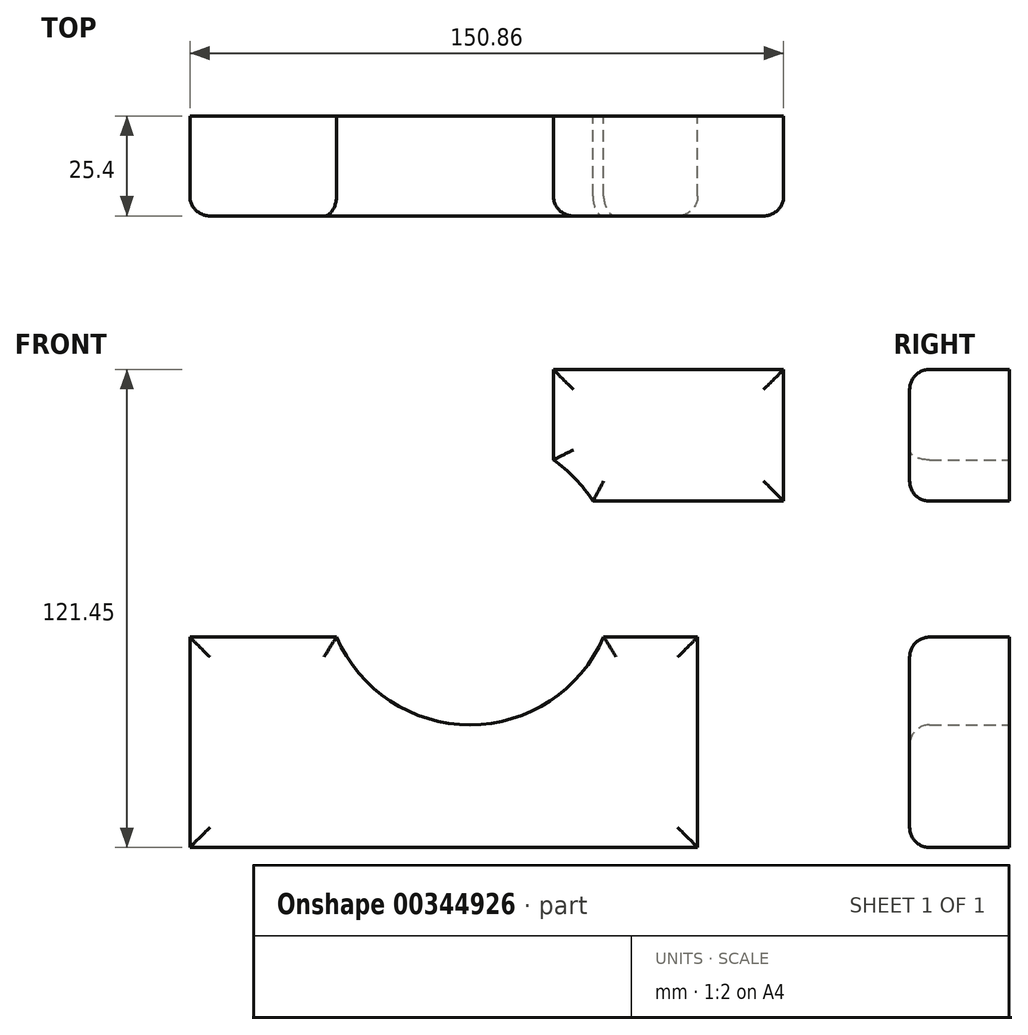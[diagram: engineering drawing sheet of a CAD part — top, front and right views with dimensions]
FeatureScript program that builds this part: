
annotation { "Feature Type Name" : "Feature", "Feature Type Description" : "" }
export const myFeature = defineFeature(function(context is Context, id is Id, definition is map)
    precondition{}
    {
        {
            var Q0;
            Q0=qCreatedBy(makeId("Front.planeOp"),FACE);
            var sketch = newSketch(context, id + "F0", { "sketchPlane" : qUnion([Q0])});
            skLineSegment(sketch, "E0.bottom", {"start": v(-71.2, -68.14) * mm, "end": v(57.8, -68.14) * mm});
            skLineSegment(sketch, "E0.top", {"start": v(-71.2, -14.68) * mm, "end": v(57.8, -14.68) * mm});
            skLineSegment(sketch, "E0.left", {"start": v(-71.2, -68.14) * mm, "end": v(-71.2, -14.68) * mm});
            skLineSegment(sketch, "E0.right", {"start": v(57.8, -68.14) * mm, "end": v(57.8, -14.68) * mm});
            skLineSegment(sketch, "E1.bottom", {"start": v(21.15, 19.85) * mm, "end": v(79.66, 19.85) * mm});
            skLineSegment(sketch, "E1.top", {"start": v(21.15, 53.31) * mm, "end": v(79.66, 53.31) * mm});
            skLineSegment(sketch, "E1.left", {"start": v(21.15, 19.85) * mm, "end": v(21.15, 53.31) * mm});
            skLineSegment(sketch, "E1.right", {"start": v(79.66, 19.85) * mm, "end": v(79.66, 53.31) * mm});
            skCircle(sketch, "E2", {"center": v(0, 0) * mm, "radius": 36.97 * mm});
            skSolve(sketch);
        }
        {
            var Q0;
            {var subQ2=sQuery(id+"F0.wireOp",EDGE,"E1.top");Q0=makeQuery(id+"F0.imprint","IMPRINT",FACE,{"disambiguationData":[TD([[makeQuery(id+"F0.imprint","IMPRINT",EDGE,{"derivedFrom":subQ2}),-1.0]])]});}
            var Q1;
            Q1=makeQuery(id+"F0.imprint","IMPRINT",FACE,{"disambiguationData":[TD([[makeQuery(id+"F0.imprint","IMPRINT",EDGE,{"derivedFrom":sQuery(id+"F0.wireOp",EDGE,"E0.bottom")}),1.0]])]});
            extrude(context, id + "F1", {"entities" : qUnion([Q0, Q1]), "endBound" : BoundingType.SYMMETRIC, "depth" : 25.4 * mm});
        }
        {
            var Q0;
            {var subQ0=sQuery(id+"F0.wireOp",EDGE,"E0.top");Q0=makeQuery(id+"F1.opExtrude","CAP_EDGE",EDGE,{"disambiguationData":[OSD([subQ0]),TDD([makeQuery(id+"F0.imprint","IMPRINT",EDGE,{"disambiguationData":[TD([[makeQuery(id+"F0.imprint","INTERSECT",VERTEX,{"derivedFrom":[subQ0,sQuery(id+"F0.wireOp",EDGE,"E0.left")]}),-1.0]])],"derivedFrom":subQ0})])],"isStart":false});}
            var Q1;
            {var subQ0=sQuery(id+"F0.wireOp",EDGE,"E2");var subQ1=sQuery(id+"F0.wireOp",EDGE,"E0.top");Q1=makeQuery(id+"F1.opExtrude","CAP_EDGE",EDGE,{"disambiguationData":[OSD([subQ0]),TDD([makeQuery(id+"F0.imprint","IMPRINT",EDGE,{"disambiguationData":[TD([[makeQuery(id+"F0.imprint","INTERSECT",VERTEX,{"disambiguationData":[OD(0.0)],"derivedFrom":[subQ1,subQ0]}),-1.0]])],"derivedFrom":subQ0})])],"isStart":false});}
            var Q2;
            {var subQ0=sQuery(id+"F0.wireOp",EDGE,"E0.top");Q2=makeQuery(id+"F1.opExtrude","CAP_EDGE",EDGE,{"disambiguationData":[OSD([subQ0]),TDD([makeQuery(id+"F0.imprint","IMPRINT",EDGE,{"disambiguationData":[TD([[makeQuery(id+"F0.imprint","INTERSECT",VERTEX,{"derivedFrom":[subQ0,sQuery(id+"F0.wireOp",EDGE,"E0.right")]}),1.0]])],"derivedFrom":subQ0})])],"isStart":false});}
            var Q3;
            {var subQ0=sQuery(id+"F0.wireOp",EDGE,"E2");Q3=makeQuery(id+"F1.opExtrude","CAP_EDGE",EDGE,{"disambiguationData":[OSD([subQ0]),TDD([makeQuery(id+"F0.imprint","IMPRINT",EDGE,{"disambiguationData":[TD([[makeQuery(id+"F0.imprint","INTERSECT",VERTEX,{"derivedFrom":[sQuery(id+"F0.wireOp",EDGE,"E1.bottom"),subQ0]}),-1.0]])],"derivedFrom":subQ0})])],"isStart":false});}
            var Q4;
            Q4=makeQuery(id+"F1.opExtrude","CAP_EDGE",EDGE,{"disambiguationData":[OSD([sQuery(id+"F0.wireOp",EDGE,"E1.left")])],"isStart":false});
            var Q5;
            Q5=makeQuery(id+"F1.opExtrude","CAP_EDGE",EDGE,{"disambiguationData":[OSD([sQuery(id+"F0.wireOp",EDGE,"E1.bottom")])],"isStart":false});
            var Q6;
            Q6=makeQuery(id+"F1.opExtrude","CAP_EDGE",EDGE,{"disambiguationData":[OSD([sQuery(id+"F0.wireOp",EDGE,"E0.left")])],"isStart":false});
            var Q7;
            Q7=makeQuery(id+"F1.opExtrude","CAP_EDGE",EDGE,{"disambiguationData":[OSD([sQuery(id+"F0.wireOp",EDGE,"E0.right")])],"isStart":false});
            var Q8;
            Q8=makeQuery(id+"F1.opExtrude","CAP_EDGE",EDGE,{"disambiguationData":[OSD([sQuery(id+"F0.wireOp",EDGE,"E1.top")])],"isStart":false});
            var Q9;
            Q9=makeQuery(id+"F1.opExtrude","CAP_EDGE",EDGE,{"disambiguationData":[OSD([sQuery(id+"F0.wireOp",EDGE,"E1.right")])],"isStart":false});
            var Q10;
            Q10=makeQuery(id+"F1.opExtrude","CAP_FACE",FACE,{"disambiguationData":[OSD([sQuery(id+"F0.wireOp",EDGE,"E0.bottom"),sQuery(id+"F0.wireOp",EDGE,"E0.top"),sQuery(id+"F0.wireOp",EDGE,"E0.left"),sQuery(id+"F0.wireOp",EDGE,"E0.right"),sQuery(id+"F0.wireOp",EDGE,"E2")])],"isStart":false});
            fillet(context, id + "F2", {"entities" : qUnion([Q0, Q1, Q2, Q3, Q4, Q5, Q6, Q7, Q8, Q9, Q10]), "radius" : 5.08 * mm, "tangentPropagation" : true, "allowEdgeOverflow" : false});
        }
    });
